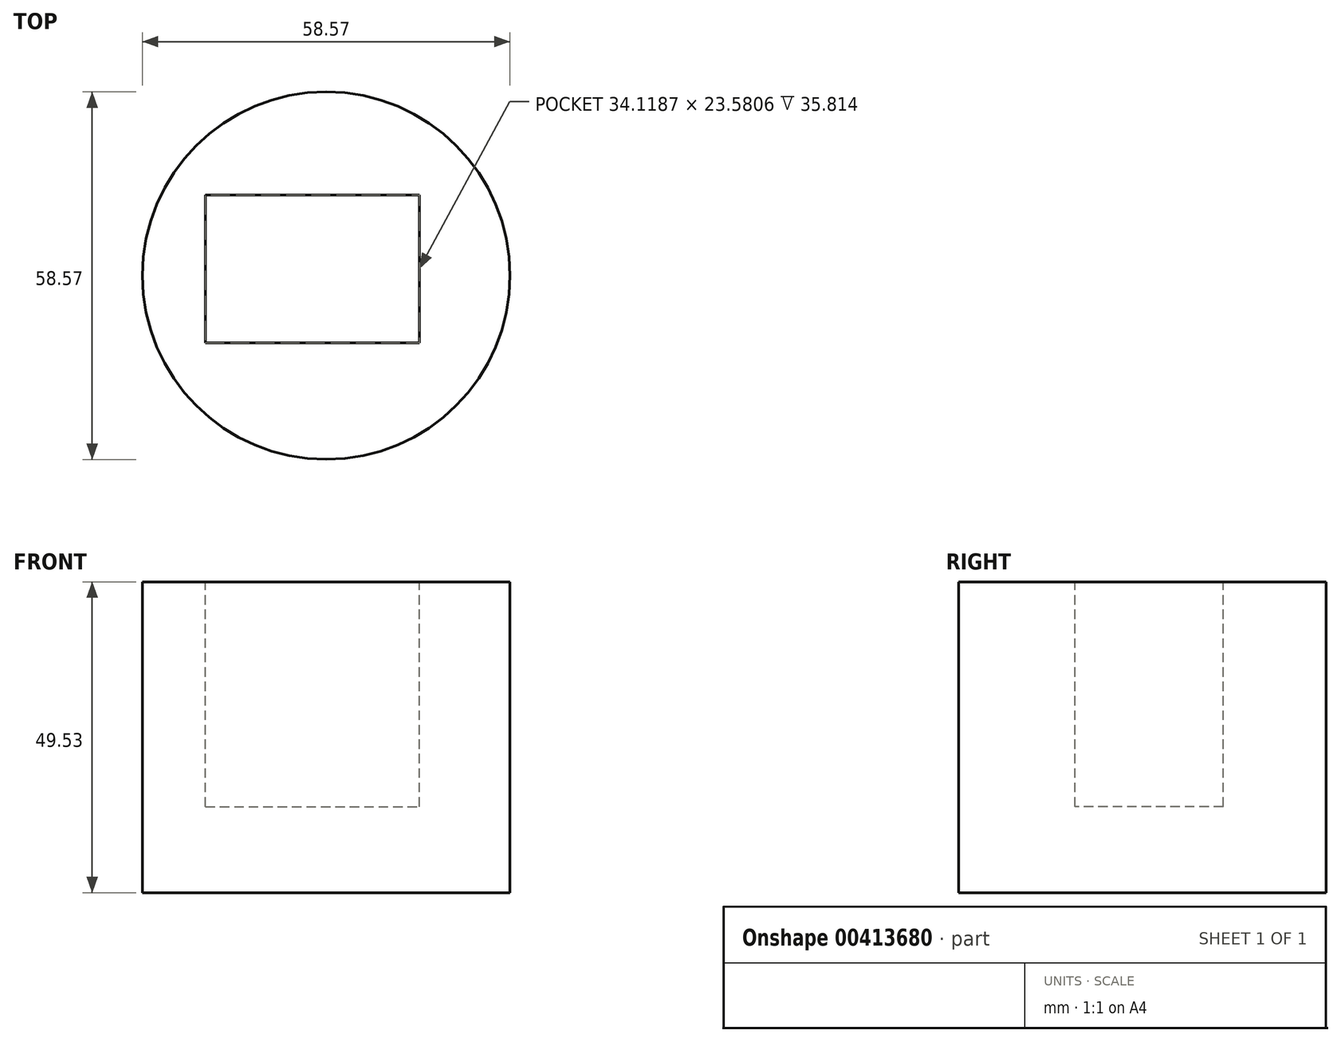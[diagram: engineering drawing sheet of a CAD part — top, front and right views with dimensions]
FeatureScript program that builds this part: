
annotation { "Feature Type Name" : "Feature", "Feature Type Description" : "" }
export const myFeature = defineFeature(function(context is Context, id is Id, definition is map)
    precondition{}
    {
        {
            var Q0;
            Q0=qCreatedBy(makeId("Top.planeOp"),FACE);
            var sketch = newSketch(context, id + "F0", { "sketchPlane" : qUnion([Q0])});
            skCircle(sketch, "E0", {"center": v(-31.14, 21.04) * mm, "radius": 29.28 * mm});
            skSolve(sketch);
        }
        {
            var Q0;
            Q0 = qSketchRegion(id + "F0", true);
            extrude(context, id + "F1", {"entities" : qUnion([Q0]), "oppositeDirection" : true, "depth" : 49.53 * mm});
        }
        {
            var Q0;
            Q0=makeQuery(id+"F1.opExtrude","CAP_FACE",FACE,{"disambiguationData":[OSD([sQuery(id+"F0.wireOp",EDGE,"E0")])],"isStart":true});
            var sketch = newSketch(context, id + "F2", { "sketchPlane" : qUnion([Q0])});
            skLineSegment(sketch, "E1.bottom", {"start": v(-50.39, 33.9) * mm, "end": v(-16.27, 33.9) * mm});
            skLineSegment(sketch, "E1.top", {"start": v(-50.39, 10.32) * mm, "end": v(-16.27, 10.32) * mm});
            skLineSegment(sketch, "E1.left", {"start": v(-50.39, 33.9) * mm, "end": v(-50.39, 10.32) * mm});
            skLineSegment(sketch, "E1.right", {"start": v(-16.27, 33.9) * mm, "end": v(-16.27, 10.32) * mm});
            skSolve(sketch);
        }
        {
            var Q0;
            Q0 = qSketchRegion(id + "F2", true);
            extrude(context, id + "F3", {"entities" : qUnion([Q0]), "operationType" : NewBodyOperationType.REMOVE, "oppositeDirection" : true, "depth" : 35.81 * mm});
        }
    });
